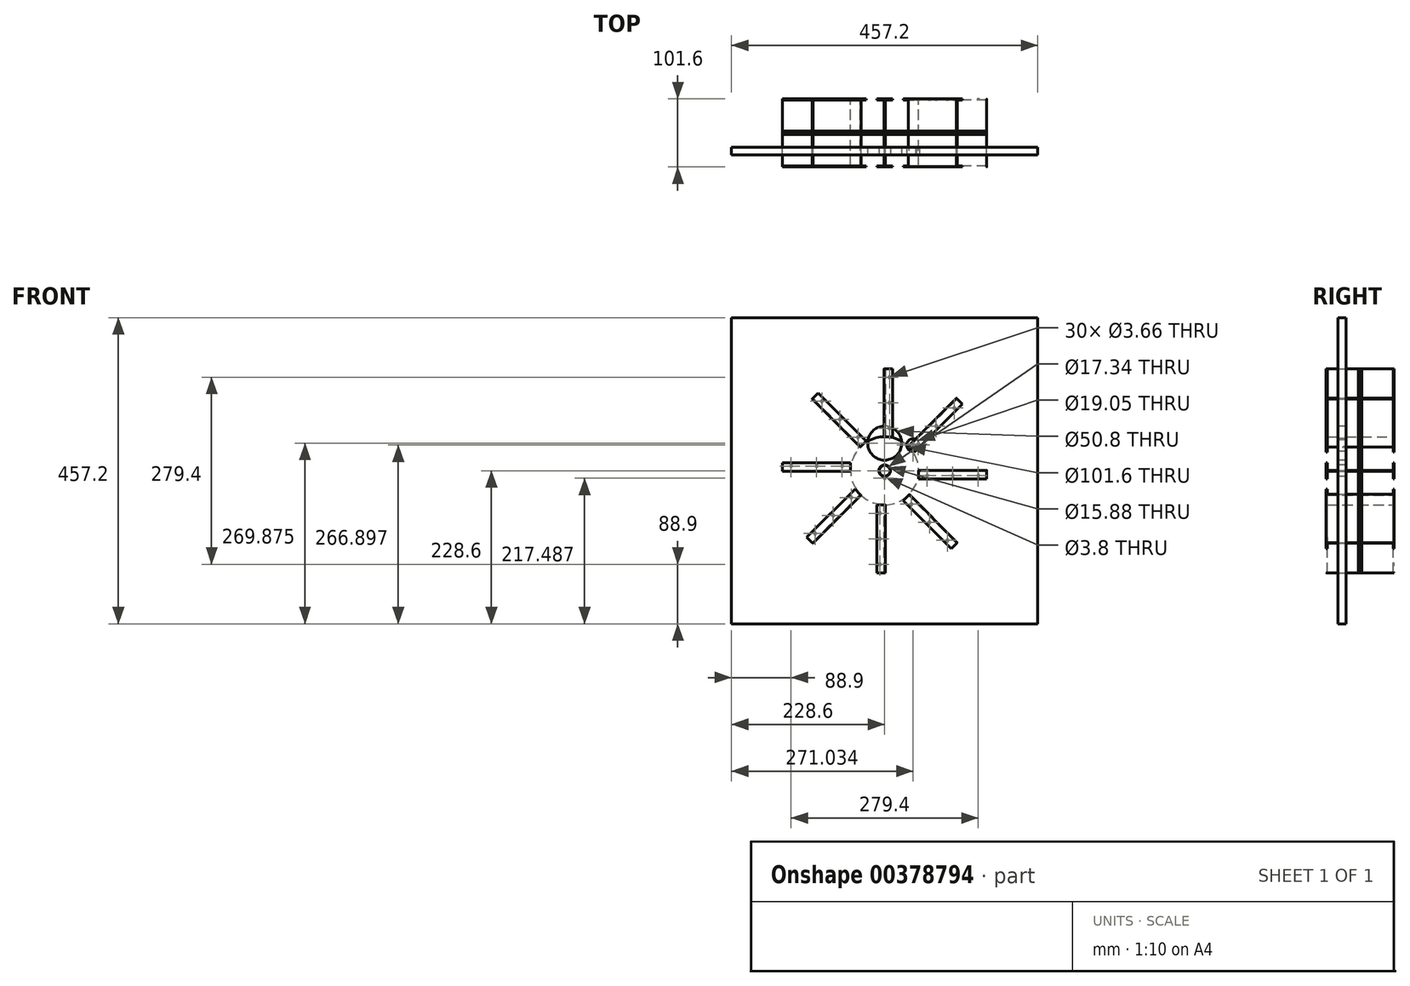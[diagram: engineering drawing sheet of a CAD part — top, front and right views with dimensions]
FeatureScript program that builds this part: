
annotation { "Feature Type Name" : "Feature", "Feature Type Description" : "" }
export const myFeature = defineFeature(function(context is Context, id is Id, definition is map)
    precondition{}
    {
        {
            assignVariable(context, id + "F0", {"name" : "Width", "anyValue" : 4});
        }
        {
            assignVariable(context, id + "F1", {"name" : "T", "anyValue" : .6});
        }
        {
            var Q0;
            Q0=qCreatedBy(makeId("Front.planeOp"),FACE);
            cPlane(context, id + "F2", {"entities" : qUnion([Q0]), "cplaneType" : CPlaneType.OFFSET, "offset" : (getVariable(context, 'Width') / 2) * mm, "width" : 152.4 * mm, "height" : 152.4 * mm});
        }
        {
            var Q0;
            Q0=qCreatedBy(makeId("Front.planeOp"),FACE);
            cPlane(context, id + "F3", {"entities" : qUnion([Q0]), "cplaneType" : CPlaneType.OFFSET, "offset" : (getVariable(context, 'Width') / 2) * mm, "oppositeDirection" : true, "width" : 152.4 * mm, "height" : 152.4 * mm});
        }
        {
            var Q0;
            Q0=qCreatedBy(makeId("Front.planeOp"),FACE);
            var sketch = newSketch(context, id + "F4", { "sketchPlane" : qUnion([Q0])});
            skCircle(sketch, "E0", {"center": v(0, 0) * mm, "radius": 152.4 * mm});
            skLineSegment(sketch, "E1", {"start": v(-19.05, 0) * mm, "end": v(19.05, 0) * mm, "construction": true});
            skArc(sketch, "E2", {"start": v(166.61, 38.1) * mm, "mid": v(170.24, 19.2) * mm, "end": v(171.45, 0) * mm});
            skArc(sketch, "E3", {"start": v(171.45, 0) * mm, "mid": v(-153.75, -134.7) * mm, "end": v(-19.05, 190.5) * mm});
            skLineSegment(sketch, "E4", {"start": v(-19.05, 190.5) * mm, "end": v(203.2, 190.5) * mm});
            skLineSegment(sketch, "E5", {"start": v(166.61, 38.1) * mm, "end": v(203.2, 38.1) * mm});
            skLineSegment(sketch, "E6.0", {"start": v(-19.05, 192.02) * mm, "end": v(203.2, 192.02) * mm});
            skArc(sketch, "E6.1", {"start": v(169.46, 36.58) * mm, "mid": v(-141.22, -148.15) * mm, "end": v(-19.05, 192.02) * mm});
            skLineSegment(sketch, "E6.2", {"start": v(169.46, 36.58) * mm, "end": v(203.2, 36.58) * mm});
            skLineSegment(sketch, "E7", {"start": v(203.2, 192.02) * mm, "end": v(203.2, 190.5) * mm});
            skLineSegment(sketch, "E8", {"start": v(203.2, 38.1) * mm, "end": v(203.2, 36.58) * mm});
            skSolve(sketch);
        }
        {
            var Q0;
            Q0=qCreatedBy(makeId("Top.planeOp"),FACE);
            cPlane(context, id + "F5", {"entities" : qUnion([Q0]), "cplaneType" : CPlaneType.OFFSET, "offset" : 50.8 * mm, "width" : 152.4 * mm, "height" : 152.4 * mm});
        }
        {
            var Q0;
            Q0=qCreatedBy(id+"F5.planeOp",FACE);
            var sketch = newSketch(context, id + "F6", { "sketchPlane" : qUnion([Q0])});
            skLineSegment(sketch, "E9", {"start": v(0, 50.8) * mm, "end": v(0, -50.8) * mm, "construction": true});
            skLineSegment(sketch, "E10", {"start": v(11.94, -50.8) * mm, "end": v(-0.76, -50.8) * mm});
            skLineSegment(sketch, "E11", {"start": v(-0.76, -50.8) * mm, "end": v(-0.76, 50.8) * mm});
            skLineSegment(sketch, "E12", {"start": v(-0.76, 50.8) * mm, "end": v(11.94, 50.8) * mm});
            skLineSegment(sketch, "E13.0", {"start": v(0.76, 49.28) * mm, "end": v(11.94, 49.28) * mm});
            skLineSegment(sketch, "E13.1", {"start": v(0.76, -49.28) * mm, "end": v(0.76, 49.28) * mm});
            skLineSegment(sketch, "E13.2", {"start": v(11.94, -49.28) * mm, "end": v(0.76, -49.28) * mm});
            skLineSegment(sketch, "E14", {"start": v(11.94, 50.8) * mm, "end": v(11.94, 49.28) * mm});
            skLineSegment(sketch, "E15", {"start": v(11.94, -50.8) * mm, "end": v(11.94, -49.28) * mm});
            skSolve(sketch);
        }
        {
            var Q0;
            Q0=qCreatedBy(id+"F3.planeOp",FACE);
            var sketch = newSketch(context, id + "F7", { "sketchPlane" : qUnion([Q0])});
            skCircle(sketch, "E16.0", {"center": v(0, 0) * mm, "radius": 152.4 * mm});
            skCircle(sketch, "E17", {"center": v(0, 0) * mm, "radius": 7.94 * mm});
            skSolve(sketch);
        }
        {
            var Q0;
            Q0 = qSketchRegion(id + "F7", true);
            extrude(context, id + "F8", {"entities" : qUnion([Q0]), "oppositeDirection" : true, "depth" : (getVariable(context, 'T')) * mm});
        }
        {
            var Q0;
            Q0=qCreatedBy(id+"F2.planeOp",FACE);
            var sketch = newSketch(context, id + "F9", { "sketchPlane" : qUnion([Q0])});
            skCircle(sketch, "E18.0", {"center": v(0, 0) * mm, "radius": 152.4 * mm});
            skCircle(sketch, "E19", {"center": v(0, 0) * mm, "radius": 50.8 * mm});
            skSolve(sketch);
        }
        {
            var Q0;
            Q0=makeQuery(id+"F9.imprint","IMPRINT",FACE,{"disambiguationData":[TD([[makeQuery(id+"F9.imprint","IMPRINT",EDGE,{"derivedFrom":sQuery(id+"F9.wireOp",EDGE,"E18.0")}),1.0]])]});
            extrude(context, id + "F10", {"entities" : qUnion([Q0]), "depth" : (getVariable(context, 'T')) * mm});
        }
        {
            var Q0;
            Q0=qCreatedBy(id+"F2.planeOp",FACE);
            cPlane(context, id + "F11", {"entities" : qUnion([Q0]), "cplaneType" : CPlaneType.OFFSET, "offset" : 19.05 * mm, "width" : 152.4 * mm, "height" : 152.4 * mm});
        }
        {
            var Q0;
            Q0=makeQuery(id+"F6.imprint","IMPRINT",FACE,{"disambiguationData":[TD([[makeQuery(id+"F6.imprint","IMPRINT",EDGE,{"derivedFrom":sQuery(id+"F6.wireOp",EDGE,"E10")}),-1.0]])]});
            extrude(context, id + "F12", {"entities" : qUnion([Q0]), "depth" : 101.6 * mm});
        }
        {
            var Q0;
            Q0=makeQuery(id+"F12.opExtrude","SWEPT_EDGE",EDGE,{"disambiguationData":[OSD([sQuery(id+"F6.wireOp",EDGE,"E13.0"),sQuery(id+"F6.wireOp",EDGE,"E13.1")])]});
            var Q1;
            Q1=makeQuery(id+"F12.opExtrude","SWEPT_EDGE",EDGE,{"disambiguationData":[OSD([sQuery(id+"F6.wireOp",EDGE,"E13.1"),sQuery(id+"F6.wireOp",EDGE,"E13.2")])]});
            fillet(context, id + "F13", {"entities" : qUnion([Q0, Q1]), "radius" : (getVariable(context, 'T')) * mm, "tangentPropagation" : true, "allowEdgeOverflow" : false});
        }
        {
            var Q0;
            Q0=makeQuery(id+"F12.opExtrude","SWEPT_EDGE",EDGE,{"disambiguationData":[OSD([sQuery(id+"F6.wireOp",EDGE,"E10"),sQuery(id+"F6.wireOp",EDGE,"E11")])]});
            var Q1;
            Q1=makeQuery(id+"F12.opExtrude","SWEPT_EDGE",EDGE,{"disambiguationData":[OSD([sQuery(id+"F6.wireOp",EDGE,"E11"),sQuery(id+"F6.wireOp",EDGE,"E12")])]});
            fillet(context, id + "F14", {"entities" : qUnion([Q0, Q1]), "radius" : (getVariable(context, 'T') * 2) * mm, "tangentPropagation" : true, "allowEdgeOverflow" : false});
        }
        {
            var Q0;
            Q0=makeQuery(id+"F10.opExtrude","CAP_FACE",FACE,{"disambiguationData":[OSD([sQuery(id+"F9.wireOp",EDGE,"E18.0"),sQuery(id+"F9.wireOp",EDGE,"E19")])],"isStart":false});
            var sketch = newSketch(context, id + "F15", { "sketchPlane" : qUnion([Q0])});
            skLineSegment(sketch, "E20.0", {"start": v(11.94, 152.4) * mm, "end": v(2.29, 152.4) * mm, "construction": true});
            skLineSegment(sketch, "E21.0", {"start": v(11.94, 50.8) * mm, "end": v(2.29, 50.8) * mm, "construction": true});
            skLineSegment(sketch, "E22", {"start": v(7.11, 50.8) * mm, "end": v(7.11, 152.4) * mm, "construction": true});
            skPoint(sketch, "E23", {"position": v(7.11, 101.6) * mm});
            skPoint(sketch, "E24", {"position": v(7.11, 63.5) * mm});
            skPoint(sketch, "E25", {"position": v(7.11, 139.7) * mm});
            skLineSegment(sketch, "E26", {"start": v(7.11, 101.6) * mm, "end": v(40.43, 101.6) * mm, "construction": true});
            skSolve(sketch);
        }
        {
            var Q0;
            Q0=sQuery(id+"F15.wireOp",VERTEX,"E24");
            var Q1;
            Q1=sQuery(id+"F15.wireOp",VERTEX,"E23");
            var Q2;
            Q2=sQuery(id+"F15.wireOp",VERTEX,"E25");
            var Q3;
            Q3=makeQuery(id+"F8.opExtrude","SWEPT_BODY",BODY,{"disambiguationData":[OSD([sQuery(id+"F7.wireOp",EDGE,"E16.0"),sQuery(id+"F7.wireOp",EDGE,"E17")])]});
            var Q4;
            Q4=makeQuery(id+"F10.opExtrude","SWEPT_BODY",BODY,{"disambiguationData":[OSD([sQuery(id+"F9.wireOp",EDGE,"E18.0"),sQuery(id+"F9.wireOp",EDGE,"E19")])]});
            var Q5;
            Q5=makeQuery(id+"F12.opExtrude","SWEPT_BODY",BODY,{"disambiguationData":[OSD([sQuery(id+"F6.wireOp",EDGE,"E10"),sQuery(id+"F6.wireOp",EDGE,"E11"),sQuery(id+"F6.wireOp",EDGE,"E12"),sQuery(id+"F6.wireOp",EDGE,"E13.0"),sQuery(id+"F6.wireOp",EDGE,"E13.1"),sQuery(id+"F6.wireOp",EDGE,"E13.2"),sQuery(id+"F6.wireOp",EDGE,"E14"),sQuery(id+"F6.wireOp",EDGE,"E15")])]});
            hole(context, id + "F16", {"style" : HoleStyle.SIMPLE, "endStyle" : HoleEndStyle.THROUGH, "standardTappedOrClearance" : lookupTablePath({ "standard" : "ANSI", "fit" : "Close", "size" : "#6", "type" : "Clearance" }), "standardBlindInLast" : lookupTablePath({ "fit" : "Close", "standard" : "ANSI", "size" : "#6", "type" : "Clearance" }), "holeDiameter" : 3.66 * mm, "isTappedThrough" : true, "tappedDepth" : 12.7 * mm, "tapClearance" : 3, "locations" : qUnion([Q0, Q1, Q2]), "scope" : qUnion([Q3, Q4, Q5])});
        }
        {
            var Q0;
            Q0=qCreatedBy(makeId("Top.planeOp"),FACE);
            var sketch = newSketch(context, id + "F17", { "sketchPlane" : qUnion([Q0])});
            skLineSegment(sketch, "E27", {"start": v(0, -164.55) * mm, "end": v(0, 164.55) * mm});
            skSolve(sketch);
        }
        {
            var Q0;
            Q0=makeQuery(id+"F12.opExtrude","SWEPT_BODY",BODY,{"disambiguationData":[OSD([sQuery(id+"F6.wireOp",EDGE,"E10"),sQuery(id+"F6.wireOp",EDGE,"E11"),sQuery(id+"F6.wireOp",EDGE,"E12"),sQuery(id+"F6.wireOp",EDGE,"E13.0"),sQuery(id+"F6.wireOp",EDGE,"E13.1"),sQuery(id+"F6.wireOp",EDGE,"E13.2"),sQuery(id+"F6.wireOp",EDGE,"E14"),sQuery(id+"F6.wireOp",EDGE,"E15")])]});
            var Q1;
            Q1=sQuery(id+"F17.wireOp",EDGE,"E27");
            circularPattern(context, id + "F18", {"entities" : qUnion([Q0]), "axis" : qUnion([Q1]), "angle" : 360 * degree, "instanceCount" : 8, "equalSpace" : true});
        }
        {
            var Q0;
            Q0=makeQuery(id+"F8.opExtrude","CAP_FACE",FACE,{"disambiguationData":[OSD([sQuery(id+"F7.wireOp",EDGE,"E16.0"),sQuery(id+"F7.wireOp",EDGE,"E17")])],"isStart":true});
            var sketch = newSketch(context, id + "F19", { "sketchPlane" : qUnion([Q0])});
            skPoint(sketch, "E28", {"position": v(0, -11.11) * mm});
            skSolve(sketch);
        }
        {
            var Q0;
            Q0=sQuery(id+"F19.wireOp",VERTEX,"E28");
            var Q1;
            Q1=makeQuery(id+"F8.opExtrude","SWEPT_BODY",BODY,{"disambiguationData":[OSD([sQuery(id+"F7.wireOp",EDGE,"E16.0"),sQuery(id+"F7.wireOp",EDGE,"E17")])]});
            hole(context, id + "F20", {"style" : HoleStyle.SIMPLE, "endStyle" : HoleEndStyle.THROUGH, "standardTappedOrClearance" : lookupTablePath({ "standard" : "ANSI", "fit" : "Normal (ASME)", "size" : "#6", "type" : "Clearance" }), "standardBlindInLast" : lookupTablePath({ "fit" : "Free", "standard" : "ANSI", "size" : "#6", "type" : "Clearance" }), "holeDiameter" : 3.8 * mm, "isTappedThrough" : true, "tappedDepth" : 12.7 * mm, "tapClearance" : 3, "locations" : qUnion([Q0]), "scope" : qUnion([Q1])});
        }
        {
            var Q0;
            Q0=qCreatedBy(id+"F11.planeOp",FACE);
            var sketch = newSketch(context, id + "F21", { "sketchPlane" : qUnion([Q0])});
            skLineSegment(sketch, "E29.bottom", {"start": v(228.6, 228.6) * mm, "end": v(-228.6, 228.6) * mm});
            skLineSegment(sketch, "E29.top", {"start": v(228.6, -228.6) * mm, "end": v(-228.6, -228.6) * mm});
            skLineSegment(sketch, "E29.left", {"start": v(228.6, 228.6) * mm, "end": v(228.6, -228.6) * mm});
            skLineSegment(sketch, "E29.right", {"start": v(-228.6, 228.6) * mm, "end": v(-228.6, -228.6) * mm});
            skPoint(sketch, "E29.middle", {"position": v(0, 0) * mm});
            skSolve(sketch);
        }
        {
            var Q0;
            Q0 = qSketchRegion(id + "F21", true);
            extrude(context, id + "F22", {"entities" : qUnion([Q0]), "depth" : 11.9 * mm});
        }
        {
            var Q0;
            Q0=makeQuery(id+"F22.opExtrude","CAP_FACE",FACE,{"disambiguationData":[OSD([sQuery(id+"F21.wireOp",EDGE,"E29.bottom"),sQuery(id+"F21.wireOp",EDGE,"E29.top"),sQuery(id+"F21.wireOp",EDGE,"E29.left"),sQuery(id+"F21.wireOp",EDGE,"E29.right")])],"isStart":false});
            var sketch = newSketch(context, id + "F23", { "sketchPlane" : qUnion([Q0])});
            skCircle(sketch, "E30", {"center": v(0, 0) * mm, "radius": 8.67 * mm});
            skSolve(sketch);
        }
        {
            var Q0;
            Q0=makeQuery(id+"F23.imprint","IMPRINT",FACE,{"disambiguationData":[TD([[makeQuery(id+"F23.imprint","IMPRINT",EDGE,{"derivedFrom":sQuery(id+"F23.wireOp",EDGE,"E30")}),1.0]])]});
            extrude(context, id + "F24", {"entities" : qUnion([Q0]), "operationType" : NewBodyOperationType.REMOVE, "endBound" : BoundingType.UP_TO_NEXT, "oppositeDirection" : true, "depth" : 25.4 * mm});
        }
        {
            var Q0;
            Q0=makeQuery(id+"F22.opExtrude","CAP_FACE",FACE,{"disambiguationData":[OSD([sQuery(id+"F21.wireOp",EDGE,"E29.bottom"),sQuery(id+"F21.wireOp",EDGE,"E29.top"),sQuery(id+"F21.wireOp",EDGE,"E29.left"),sQuery(id+"F21.wireOp",EDGE,"E29.right")])],"isStart":false});
            var sketch = newSketch(context, id + "F25", { "sketchPlane" : qUnion([Q0])});
            skCircle(sketch, "E31", {"center": v(0, 0) * mm, "radius": 76.2 * mm, "construction": true});
            skCircle(sketch, "E32", {"center": v(0, 0) * mm, "radius": 66.67 * mm, "construction": true});
            skCircle(sketch, "E33.0", {"center": v(0, 0) * mm, "radius": 8.67 * mm, "construction": true});
            skLineSegment(sketch, "E34", {"start": v(0, 8.67) * mm, "end": v(0, 66.67) * mm, "construction": true});
            skCircle(sketch, "E35", {"center": v(0, 41.27) * mm, "radius": 25.4 * mm});
            skLineSegment(sketch, "E36", {"start": v(7.84, 3.7) * mm, "end": v(49.17, 45.03) * mm});
            skCircle(sketch, "E37", {"center": v(42.43, 38.3) * mm, "radius": 9.53 * mm});
            skSolve(sketch);
        }
        {
            var Q0;
            Q0=makeQuery(id+"F25.imprint","IMPRINT",FACE,{"disambiguationData":[TD([[makeQuery(id+"F25.imprint","IMPRINT",EDGE,{"derivedFrom":sQuery(id+"F25.wireOp",EDGE,"E35")}),1.0]])]});
            var Q1;
            {var subQ0=sQuery(id+"F25.wireOp",EDGE,"E37");var subQ1=sQuery(id+"F25.wireOp",EDGE,"E36");var subQ2=makeQuery(id+"F25.imprint","INTERSECT",VERTEX,{"disambiguationData":[OD(0.0)],"derivedFrom":[subQ1,subQ0]});Q1=makeQuery(id+"F25.imprint","IMPRINT",FACE,{"disambiguationData":[TD([[makeQuery(id+"F25.imprint","IMPRINT",EDGE,{"disambiguationData":[TD([[subQ2,1.0]])],"derivedFrom":subQ1}),1.0]])]});}
            var Q2;
            {var subQ0=sQuery(id+"F25.wireOp",EDGE,"E37");var subQ1=sQuery(id+"F25.wireOp",EDGE,"E36");var subQ2=makeQuery(id+"F25.imprint","INTERSECT",VERTEX,{"disambiguationData":[OD(0.0)],"derivedFrom":[subQ1,subQ0]});Q2=makeQuery(id+"F25.imprint","IMPRINT",FACE,{"disambiguationData":[TD([[makeQuery(id+"F25.imprint","IMPRINT",EDGE,{"disambiguationData":[TD([[subQ2,1.0]])],"derivedFrom":subQ1}),-1.0]])]});}
            extrude(context, id + "F26", {"entities" : qUnion([Q0, Q1, Q2]), "operationType" : NewBodyOperationType.REMOVE, "endBound" : BoundingType.UP_TO_NEXT, "oppositeDirection" : true, "depth" : 25.4 * mm});
        }
    });
